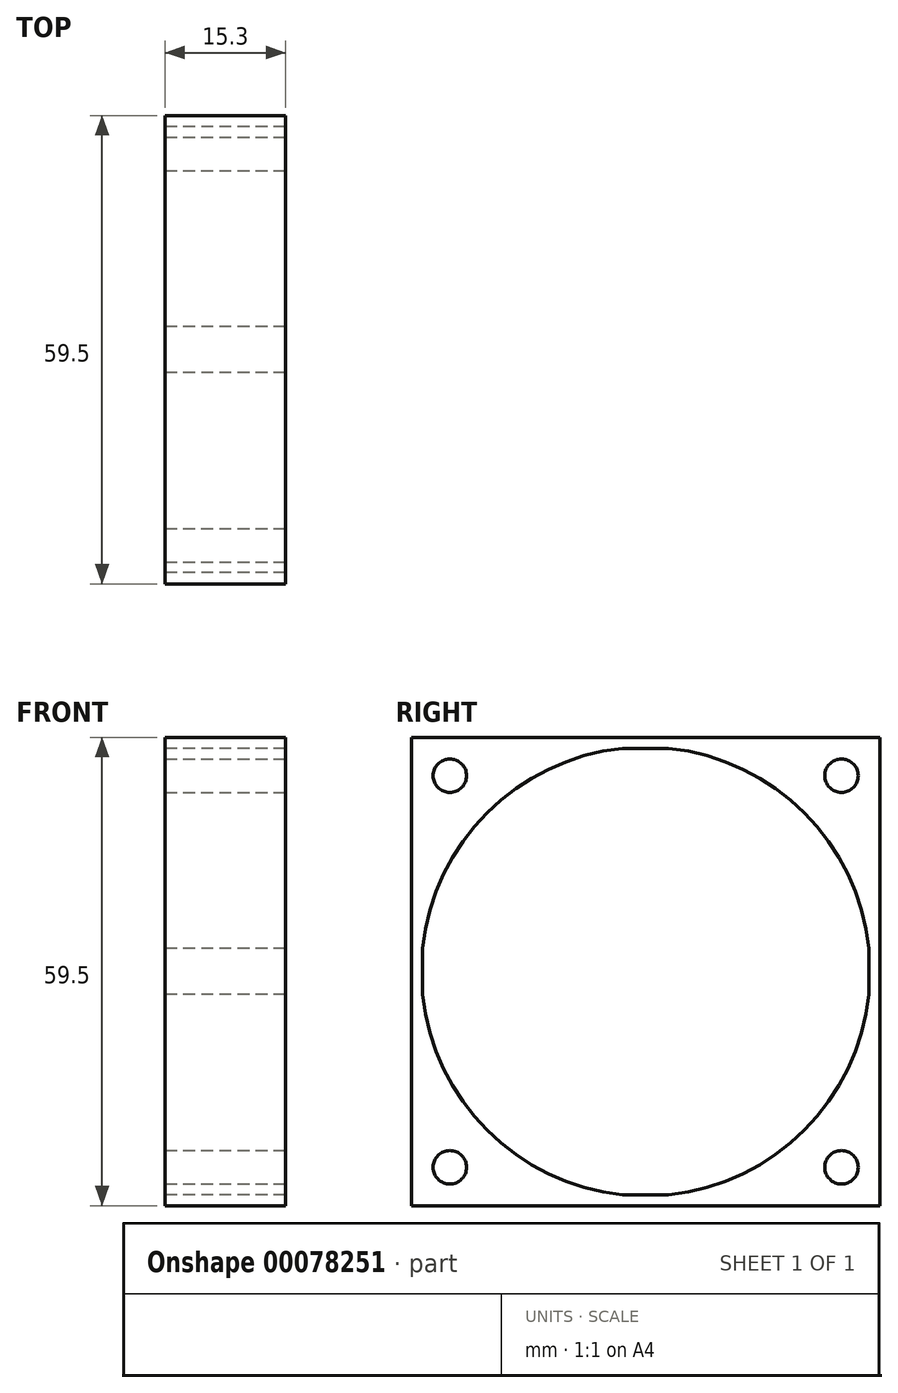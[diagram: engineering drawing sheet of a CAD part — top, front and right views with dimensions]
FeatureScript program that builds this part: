
annotation { "Feature Type Name" : "Feature", "Feature Type Description" : "" }
export const myFeature = defineFeature(function(context is Context, id is Id, definition is map)
    precondition{}
    {
        {
            var Q0;
            Q0=qCreatedBy(makeId("Right.planeOp"),FACE);
            var sketch = newSketch(context, id + "F0", { "sketchPlane" : qUnion([Q0])});
            skLineSegment(sketch, "E0.bottom", {"start": v(29.75, 29.75) * mm, "end": v(-29.75, 29.75) * mm});
            skLineSegment(sketch, "E0.top", {"start": v(29.75, -29.75) * mm, "end": v(-29.75, -29.75) * mm});
            skLineSegment(sketch, "E0.left", {"start": v(29.75, 29.75) * mm, "end": v(29.75, -29.75) * mm});
            skLineSegment(sketch, "E0.right", {"start": v(-29.75, 29.75) * mm, "end": v(-29.75, -29.75) * mm});
            skPoint(sketch, "E0.middle", {"position": v(0, 0) * mm});
            skArc(sketch, "E1", {"start": v(-28.35, -2.92) * mm, "mid": v(-20.15, -20.15) * mm, "end": v(-2.92, -28.35) * mm});
            skLineSegment(sketch, "E2.bottom", {"start": v(2.92, -28.35) * mm, "end": v(-2.92, -28.35) * mm});
            skLineSegment(sketch, "E2.top", {"start": v(2.92, 28.35) * mm, "end": v(-2.92, 28.35) * mm});
            skLineSegment(sketch, "E2.left", {"start": v(28.35, -2.92) * mm, "end": v(28.35, 2.92) * mm});
            skLineSegment(sketch, "E2.right", {"start": v(-28.35, -2.92) * mm, "end": v(-28.35, 2.92) * mm});
            skPoint(sketch, "E3.orphan", {"position": v(-28.35, 28.35) * mm});
            skPoint(sketch, "E4.orphan", {"position": v(28.35, 28.35) * mm});
            skPoint(sketch, "E5.orphan", {"position": v(28.35, -28.35) * mm});
            skPoint(sketch, "E6.orphan", {"position": v(-28.35, -28.35) * mm});
            skArc(sketch, "E7.trimOffspring", {"start": v(2.92, -28.35) * mm, "mid": v(20.15, -20.15) * mm, "end": v(28.35, -2.92) * mm});
            skArc(sketch, "E8.trimOffspring", {"start": v(28.35, 2.92) * mm, "mid": v(20.15, 20.15) * mm, "end": v(2.92, 28.35) * mm});
            skArc(sketch, "E9.trimOffspring", {"start": v(-2.92, 28.35) * mm, "mid": v(-20.15, 20.15) * mm, "end": v(-28.35, 2.92) * mm});
            skSolve(sketch);
        }
        {
            var Q0;
            Q0 = qSketchRegion(id + "F0", true);
            extrude(context, id + "F1", {"entities" : qUnion([Q0]), "depth" : 15.3 * mm});
        }
        {
            var Q0;
            Q0=makeQuery(id+"F1.opExtrude","CAP_FACE",FACE,{"disambiguationData":[OSD([sQuery(id+"F0.wireOp",EDGE,"E0.bottom"),sQuery(id+"F0.wireOp",EDGE,"E0.top"),sQuery(id+"F0.wireOp",EDGE,"E0.left"),sQuery(id+"F0.wireOp",EDGE,"E0.right"),sQuery(id+"F0.wireOp",EDGE,"E1"),sQuery(id+"F0.wireOp",EDGE,"E2.bottom"),sQuery(id+"F0.wireOp",EDGE,"E2.top"),sQuery(id+"F0.wireOp",EDGE,"E2.left"),sQuery(id+"F0.wireOp",EDGE,"E2.right"),sQuery(id+"F0.wireOp",EDGE,"E7.trimOffspring"),sQuery(id+"F0.wireOp",EDGE,"E8.trimOffspring"),sQuery(id+"F0.wireOp",EDGE,"E9.trimOffspring")])],"isStart":false});
            var sketch = newSketch(context, id + "F2", { "sketchPlane" : qUnion([Q0])});
            skLineSegment(sketch, "E10", {"start": v(-29.75, 29.75) * mm, "end": v(29.75, -29.75) * mm, "construction": true});
            skLineSegment(sketch, "E11.bottom", {"start": v(24.87, 24.87) * mm, "end": v(-24.87, 24.87) * mm, "construction": true});
            skLineSegment(sketch, "E11.top", {"start": v(24.87, -24.87) * mm, "end": v(-24.87, -24.87) * mm, "construction": true});
            skLineSegment(sketch, "E11.left", {"start": v(24.87, 24.87) * mm, "end": v(24.87, -24.87) * mm, "construction": true});
            skLineSegment(sketch, "E11.right", {"start": v(-24.87, 24.87) * mm, "end": v(-24.87, -24.87) * mm, "construction": true});
            skPoint(sketch, "E11.middle", {"position": v(0, 0) * mm});
            skCircle(sketch, "E12", {"center": v(-24.87, 24.87) * mm, "radius": 2.12 * mm});
            skLineSegment(sketch, "E13.0.1.0", {"start": v(24.87, -74.62) * mm, "end": v(-24.87, -74.62) * mm, "construction": true});
            skCircle(sketch, "E13.0.1.1", {"center": v(-24.87, -24.88) * mm, "radius": 2.12 * mm});
            skLineSegment(sketch, "E13.1.0.0", {"start": v(74.62, -24.87) * mm, "end": v(24.87, -24.87) * mm, "construction": true});
            skCircle(sketch, "E13.1.0.1", {"center": v(24.87, 24.87) * mm, "radius": 2.12 * mm});
            skLineSegment(sketch, "E13.1.1.0", {"start": v(74.62, -74.62) * mm, "end": v(24.87, -74.62) * mm, "construction": true});
            skCircle(sketch, "E13.1.1.1", {"center": v(24.87, -24.88) * mm, "radius": 2.12 * mm});
            skLineSegment(sketch, "E13.direction1", {"start": v(-24.87, -24.87) * mm, "end": v(24.87, -24.87) * mm, "construction": true});
            skLineSegment(sketch, "E13.direction2", {"start": v(-24.87, -24.87) * mm, "end": v(-24.87, -74.62) * mm, "construction": true});
            skSolve(sketch);
        }
        {
            var Q0;
            Q0=makeQuery(id+"F2.imprint","IMPRINT",FACE,{"disambiguationData":[TD([[makeQuery(id+"F2.imprint","IMPRINT",EDGE,{"derivedFrom":sQuery(id+"F2.wireOp",EDGE,"E12")}),1.0]])]});
            var Q1;
            Q1=makeQuery(id+"F2.imprint","IMPRINT",FACE,{"disambiguationData":[TD([[makeQuery(id+"F2.imprint","IMPRINT",EDGE,{"derivedFrom":sQuery(id+"F2.wireOp",EDGE,"E13.1.0.1")}),1.0]])]});
            var Q2;
            Q2=makeQuery(id+"F2.imprint","IMPRINT",FACE,{"disambiguationData":[TD([[makeQuery(id+"F2.imprint","IMPRINT",EDGE,{"derivedFrom":sQuery(id+"F2.wireOp",EDGE,"E13.1.1.1")}),1.0]])]});
            var Q3;
            Q3=makeQuery(id+"F2.imprint","IMPRINT",FACE,{"disambiguationData":[TD([[makeQuery(id+"F2.imprint","IMPRINT",EDGE,{"derivedFrom":sQuery(id+"F2.wireOp",EDGE,"E13.0.1.1")}),1.0]])]});
            extrude(context, id + "F3", {"entities" : qUnion([Q0, Q1, Q2, Q3]), "operationType" : NewBodyOperationType.REMOVE, "oppositeDirection" : true, "depth" : 25 * mm});
        }
    });
